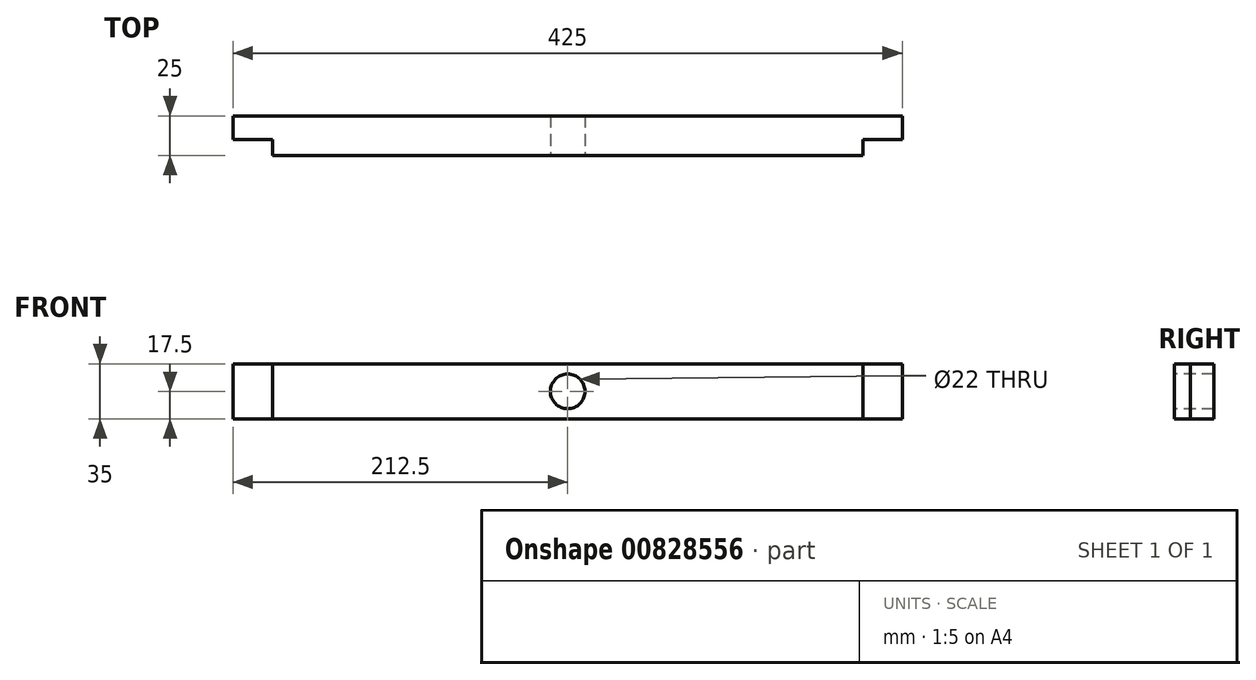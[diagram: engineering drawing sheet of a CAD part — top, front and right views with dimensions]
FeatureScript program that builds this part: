
annotation { "Feature Type Name" : "Feature", "Feature Type Description" : "" }
export const myFeature = defineFeature(function(context is Context, id is Id, definition is map)
    precondition{}
    {
        {
            var Q0;
            Q0=qCreatedBy(makeId("Front.planeOp"),FACE);
            var sketch = newSketch(context, id + "F0", { "sketchPlane" : qUnion([Q0])});
            skLineSegment(sketch, "E0.bottom", {"start": v(-212.5, 35) * mm, "end": v(212.5, 35) * mm});
            skLineSegment(sketch, "E0.top", {"start": v(-212.5, 0) * mm, "end": v(212.5, 0) * mm});
            skLineSegment(sketch, "E0.left", {"start": v(-212.5, 35) * mm, "end": v(-212.5, 0) * mm});
            skLineSegment(sketch, "E0.right", {"start": v(212.5, 35) * mm, "end": v(212.5, 0) * mm});
            skSolve(sketch);
        }
        {
            var Q0;
            Q0=qSketchRegion(id+"F0",true);
            extrude(context, id + "F1", {"entities" : qUnion([Q0]), "depth" : 15 * mm, "offsetDistance" : 25 * mm});
        }
        {
            var Q0;
            Q0=makeQuery(id+"F1.opExtrude","CAP_FACE",FACE,{"disambiguationData":[OSD([sQuery(id+"F0.wireOp",EDGE,"E0.bottom"),sQuery(id+"F0.wireOp",EDGE,"E0.top"),sQuery(id+"F0.wireOp",EDGE,"E0.left"),sQuery(id+"F0.wireOp",EDGE,"E0.right")])],"isStart":false});
            var sketch = newSketch(context, id + "F2", { "sketchPlane" : qUnion([Q0])});
            skLineSegment(sketch, "E1.bottom", {"start": v(-187.5, 35) * mm, "end": v(187.5, 35) * mm});
            skLineSegment(sketch, "E1.top", {"start": v(-187.5, 0) * mm, "end": v(187.5, 0) * mm});
            skLineSegment(sketch, "E1.left", {"start": v(-187.5, 35) * mm, "end": v(-187.5, 0) * mm});
            skLineSegment(sketch, "E1.right", {"start": v(187.5, 35) * mm, "end": v(187.5, 0) * mm});
            skSolve(sketch);
        }
        {
            var Q0;
            Q0=qSketchRegion(id+"F2",true);
            extrude(context, id + "F3", {"entities" : qUnion([Q0]), "operationType" : NewBodyOperationType.ADD, "depth" : 10 * mm, "offsetDistance" : 25 * mm});
        }
        {
            var Q0;
            Q0=makeQuery(id+"F1.opExtrude","CAP_FACE",FACE,{"disambiguationData":[OSD([sQuery(id+"F0.wireOp",EDGE,"E0.bottom"),sQuery(id+"F0.wireOp",EDGE,"E0.top"),sQuery(id+"F0.wireOp",EDGE,"E0.left"),sQuery(id+"F0.wireOp",EDGE,"E0.right")])],"isStart":true});
            var sketch = newSketch(context, id + "F4", { "sketchPlane" : qUnion([Q0])});
            skPoint(sketch, "E2", {"position": v(0, 17.5) * mm});
            skLineSegment(sketch, "E3", {"start": v(0, 17.5) * mm, "end": v(0, 35) * mm, "construction": true});
            skLineSegment(sketch, "E4", {"start": v(0, 17.5) * mm, "end": v(0, 0) * mm, "construction": true});
            skSolve(sketch);
        }
        {
            var Q0;
            Q0=sQuery(id+"F4.wireOp",VERTEX,"E2");
            var Q1;
            Q1=makeQuery(id+"F1.opExtrude","SWEPT_BODY",BODY,{"disambiguationData":[OSD([sQuery(id+"F0.wireOp",EDGE,"E0.bottom"),sQuery(id+"F0.wireOp",EDGE,"E0.top"),sQuery(id+"F0.wireOp",EDGE,"E0.left"),sQuery(id+"F0.wireOp",EDGE,"E0.right")])]});
            hole(context, id + "F5", {"style" : HoleStyle.SIMPLE, "endStyle" : HoleEndStyle.THROUGH, "holeDiameter" : 22 * mm, "majorDiameter" : 5 * mm, "isTappedThrough" : true, "tappedDepth" : 12 * mm, "tapClearance" : 3, "locations" : qUnion([Q0]), "scope" : qUnion([Q1])});
        }
    });
